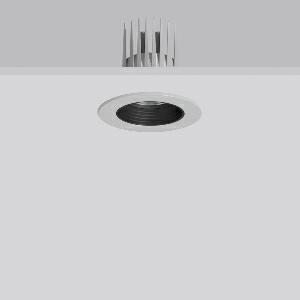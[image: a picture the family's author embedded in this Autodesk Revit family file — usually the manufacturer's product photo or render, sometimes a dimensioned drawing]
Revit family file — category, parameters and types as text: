
# Revit family: heledon_mini_e_901743_004_582b
name_source: partatom
category: Lighting Fixtures
units: mm (PartAtom-declared; Revit-internal decimal feet)

## family parameters
Cut with Voids When Loaded = No
Host = Face
Light Source = No
Part Type = Normal
Room Calculation Point = No
Round Connector Dimension = Use Diameter
Shared = No

## types (1)
- HELEDON mini E (1 x LED Modul 930, 2250 lm, 3000)
    Apparent Load = 20 VA
    Approval mark = CE
    CIE Flux Codes = 99 100 100 100 100
    Color Rendering = 90
    Color Temperature = 3000
    Default Elevation = 1800 mm
    Description = Series: HELEDON mini
Round recessed downlight. Housing: die-cast aluminium, powder-coated. Black plastic ring and recessed LED to prevent glare from the side. Optical assembly with lens made of plastic (polycarbonate) for the best homogeneous light distribution - can be changed without tools. Best colour rendering index Ra>90. Suitable for Recessed ceiling mounting. Installation without tools thanks to spring fastening system. Including separate LED converter with connecting cable 600 mm.High quality converter without flickering and stroboscopic effect. Through-wiring box (5 pole) available as accessory. The following accessories can be mounted without use of tools: interchangeable lenses, decorative glasses, honeycomb louvre, clear and frosted diffusers, white interchangeable plastic ring. 
Colour: silver
Diameter: 124 mm
Height: 3 mm
Cut-out diameter: 114 mm
Recess height: 170 mm
Luminaire: recess height: 120 mm
Lamp: LED
Socket: without socket
Colour temperature: 3000K
Colour rendering index (CRI): 92
System power: 20 W
Rated luminous flux: 2250 lm
Luminous efficiency: 113 lm/W
Control gear: Regulated power supply
Protection class: II
Type of protection: IP 20
    Height = 0 mm  [stored 0 ft]
    Lamp = 1 x LED Modul 930
    Lamp Light Flux = 2250 lm
    Lamp count = 1
    Length = 124 mm  [stored 0.406824 ft]
    Lifetime = 50000 h
    Luminous efficacy = 113 lm/W
    Manufacturer = RZB
    ModVariant = No
    Model = 901743.004
    Mounting Place = Ceiling
    Mounting Type = Recessed
    Number of Poles = 1
    OnlyDefault = Yes
    Power Factor = 1
    Product Name = HELEDON mini E
    Product group = Recessed downlights
    ProductGroupID = 402
    Protection Class = Protection class II
    Protection Degree = IP 20
    RLX_Detail_Level = 1
    RLX_Emergency_Light_Flux = 0 lm
    RLX_Emergency_Type = 0
    RLX_Emergency_Type_DB = No
    RlxData = <blob elided: 122909 chars, md5=aea464c2>
    Socket = socket
    Standby Power = 0 W
    System Light Flux = 2250 lm
    System Power = 20 W
    Type Comments = Product without accessories
    Type Image = 901656.004.jpg
    URL = http://relux.com
    VarID = ---
    Voltage = 230 V
    Voltage Range = 220-240 V
    Weight = 0.00 kg
    Width = 0 mm  [stored 0 ft]

note: [stored X ft] marks values corroborated as IEEE doubles in the binary element streams (Revit-internal decimal feet)

## geometry (parser evidence)
native form markers: Blend x4, Sweep x11
no freeform markers — native parametric forms only
